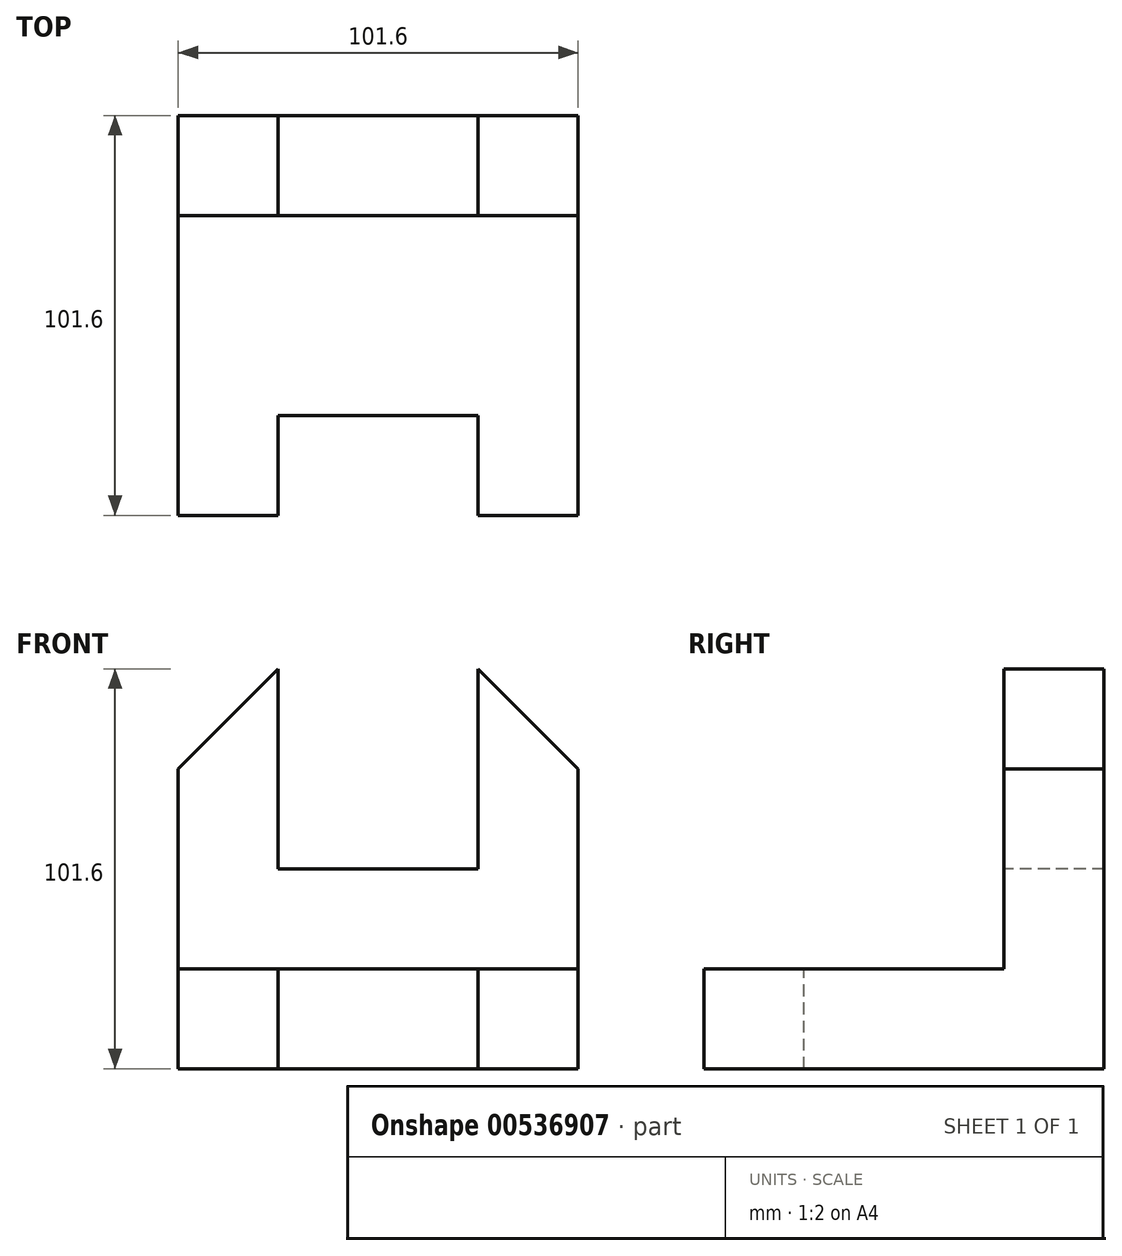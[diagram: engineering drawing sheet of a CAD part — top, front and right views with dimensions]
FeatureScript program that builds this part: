
annotation { "Feature Type Name" : "Feature", "Feature Type Description" : "" }
export const myFeature = defineFeature(function(context is Context, id is Id, definition is map)
    precondition{}
    {
        {
            var Q0;
            Q0=qCreatedBy(makeId("Front.planeOp"),FACE);
            var sketch = newSketch(context, id + "F0", { "sketchPlane" : qUnion([Q0])});
            skLineSegment(sketch, "E0.bottom", {"start": v(-56.62, 59.75) * mm, "end": v(44.98, 59.75) * mm});
            skLineSegment(sketch, "E0.top", {"start": v(-56.62, -41.85) * mm, "end": v(44.98, -41.85) * mm});
            skLineSegment(sketch, "E0.left", {"start": v(-56.62, 59.75) * mm, "end": v(-56.62, -41.85) * mm});
            skLineSegment(sketch, "E0.right", {"start": v(44.98, 59.75) * mm, "end": v(44.98, -41.85) * mm});
            skSolve(sketch);
        }
        {
            var Q0;
            Q0=qSketchRegion(id+"F0",true);
            extrude(context, id + "F1", {"entities" : qUnion([Q0]), "depth" : 101.6 * mm, "offsetDistance" : 25.4 * mm});
        }
        {
            var Q0;
            Q0=makeQuery(id+"F1.opExtrude","CAP_FACE",FACE,{"disambiguationData":[OSD([sQuery(id+"F0.wireOp",EDGE,"E0.bottom"),sQuery(id+"F0.wireOp",EDGE,"E0.top"),sQuery(id+"F0.wireOp",EDGE,"E0.left"),sQuery(id+"F0.wireOp",EDGE,"E0.right")])],"isStart":false});
            var sketch = newSketch(context, id + "F2", { "sketchPlane" : qUnion([Q0])});
            skLineSegment(sketch, "E1", {"start": v(-31.22, -41.85) * mm, "end": v(19.58, -41.85) * mm});
            skLineSegment(sketch, "E2", {"start": v(19.58, -41.85) * mm, "end": v(44.98, -41.85) * mm});
            skLineSegment(sketch, "E3", {"start": v(-31.22, -41.85) * mm, "end": v(-31.22, -16.45) * mm});
            skLineSegment(sketch, "E4", {"start": v(-31.22, -16.45) * mm, "end": v(19.58, -16.45) * mm});
            skLineSegment(sketch, "E5", {"start": v(19.58, -16.45) * mm, "end": v(19.58, -41.85) * mm});
            skSolve(sketch);
        }
        {
            var Q0;
            Q0=makeQuery(id+"F2.imprint","IMPRINT",FACE,{"disambiguationData":[TD([[makeQuery(id+"F2.imprint","IMPRINT",EDGE,{"derivedFrom":sQuery(id+"F2.wireOp",EDGE,"E1")}),1.0]])]});
            extrude(context, id + "F3", {"entities" : qUnion([Q0]), "operationType" : NewBodyOperationType.REMOVE, "oppositeDirection" : true, "depth" : 25.4 * mm, "offsetDistance" : 25.4 * mm});
        }
        {
            var Q0;
            Q0=makeQuery(id+"F1.opExtrude","CAP_FACE",FACE,{"disambiguationData":[OSD([sQuery(id+"F0.wireOp",EDGE,"E0.bottom"),sQuery(id+"F0.wireOp",EDGE,"E0.top"),sQuery(id+"F0.wireOp",EDGE,"E0.left"),sQuery(id+"F0.wireOp",EDGE,"E0.right")])],"isStart":false});
            var sketch = newSketch(context, id + "F4", { "sketchPlane" : qUnion([Q0])});
            skLineSegment(sketch, "E6.bottom", {"start": v(-56.62, -16.45) * mm, "end": v(44.98, -16.45) * mm});
            skLineSegment(sketch, "E6.top", {"start": v(-56.62, 59.75) * mm, "end": v(44.98, 59.75) * mm});
            skLineSegment(sketch, "E6.left", {"start": v(-56.62, -16.45) * mm, "end": v(-56.62, 59.75) * mm});
            skLineSegment(sketch, "E6.right", {"start": v(44.98, -16.45) * mm, "end": v(44.98, 59.75) * mm});
            skSolve(sketch);
        }
        {
            var Q0;
            Q0=qSketchRegion(id+"F4",true);
            extrude(context, id + "F5", {"entities" : qUnion([Q0]), "operationType" : NewBodyOperationType.REMOVE, "oppositeDirection" : true, "depth" : 76.2 * mm, "offsetDistance" : 25.4 * mm});
        }
        {
            var Q0;
            Q0=makeQuery(id+"F5.boolean.opBoolean","COPY",FACE,{"derivedFrom":makeQuery(id+"F5.opExtrude","CAP_FACE",FACE,{"disambiguationData":[OSD([sQuery(id+"F4.wireOp",EDGE,"E6.bottom"),sQuery(id+"F4.wireOp",EDGE,"E6.top"),sQuery(id+"F4.wireOp",EDGE,"E6.left"),sQuery(id+"F4.wireOp",EDGE,"E6.right")])],"isStart":false})});
            var sketch = newSketch(context, id + "F6", { "sketchPlane" : qUnion([Q0])});
            skLineSegment(sketch, "E7", {"start": v(-56.62, 59.75) * mm, "end": v(-31.22, 59.75) * mm});
            skLineSegment(sketch, "E8", {"start": v(-56.62, 59.75) * mm, "end": v(-56.62, 34.35) * mm});
            skLineSegment(sketch, "E9", {"start": v(-56.62, 34.35) * mm, "end": v(-31.22, 59.75) * mm});
            skLineSegment(sketch, "E10", {"start": v(19.58, 59.75) * mm, "end": v(44.98, 34.35) * mm});
            skLineSegment(sketch, "E11", {"start": v(44.98, 34.35) * mm, "end": v(44.98, 59.75) * mm});
            skLineSegment(sketch, "E12", {"start": v(44.98, 59.75) * mm, "end": v(19.58, 59.75) * mm});
            skSolve(sketch);
        }
        {
            var Q0;
            Q0=makeQuery(id+"F6.imprint","IMPRINT",FACE,{"disambiguationData":[TD([[makeQuery(id+"F6.imprint","IMPRINT",EDGE,{"derivedFrom":sQuery(id+"F6.wireOp",EDGE,"E10")}),1.0]])]});
            var Q1;
            Q1=makeQuery(id+"F6.imprint","IMPRINT",FACE,{"disambiguationData":[TD([[makeQuery(id+"F6.imprint","IMPRINT",EDGE,{"derivedFrom":sQuery(id+"F6.wireOp",EDGE,"E7")}),-1.0]])]});
            extrude(context, id + "F7", {"entities" : qUnion([Q0, Q1]), "operationType" : NewBodyOperationType.REMOVE, "oppositeDirection" : true, "depth" : 25.4 * mm, "offsetDistance" : 25.4 * mm});
        }
        {
            var Q0;
            Q0=makeQuery(id+"F5.boolean.opBoolean","COPY",FACE,{"derivedFrom":makeQuery(id+"F5.opExtrude","CAP_FACE",FACE,{"disambiguationData":[OSD([sQuery(id+"F4.wireOp",EDGE,"E6.bottom"),sQuery(id+"F4.wireOp",EDGE,"E6.top"),sQuery(id+"F4.wireOp",EDGE,"E6.left"),sQuery(id+"F4.wireOp",EDGE,"E6.right")])],"isStart":false})});
            var sketch = newSketch(context, id + "F8", { "sketchPlane" : qUnion([Q0])});
            skLineSegment(sketch, "E13.bottom", {"start": v(-31.22, 59.75) * mm, "end": v(19.58, 59.75) * mm});
            skLineSegment(sketch, "E13.top", {"start": v(-31.22, 8.95) * mm, "end": v(19.58, 8.95) * mm});
            skLineSegment(sketch, "E13.left", {"start": v(-31.22, 59.75) * mm, "end": v(-31.22, 8.95) * mm});
            skLineSegment(sketch, "E13.right", {"start": v(19.58, 59.75) * mm, "end": v(19.58, 8.95) * mm});
            skSolve(sketch);
        }
        {
            var Q0;
            Q0=makeQuery(id+"F8.imprint","IMPRINT",FACE,{"disambiguationData":[TD([[makeQuery(id+"F8.imprint","IMPRINT",EDGE,{"derivedFrom":sQuery(id+"F8.wireOp",EDGE,"E13.bottom")}),-1.0]])]});
            extrude(context, id + "F9", {"entities" : qUnion([Q0]), "operationType" : NewBodyOperationType.REMOVE, "oppositeDirection" : true, "depth" : 25.4 * mm, "offsetDistance" : 25.4 * mm});
        }
    });
